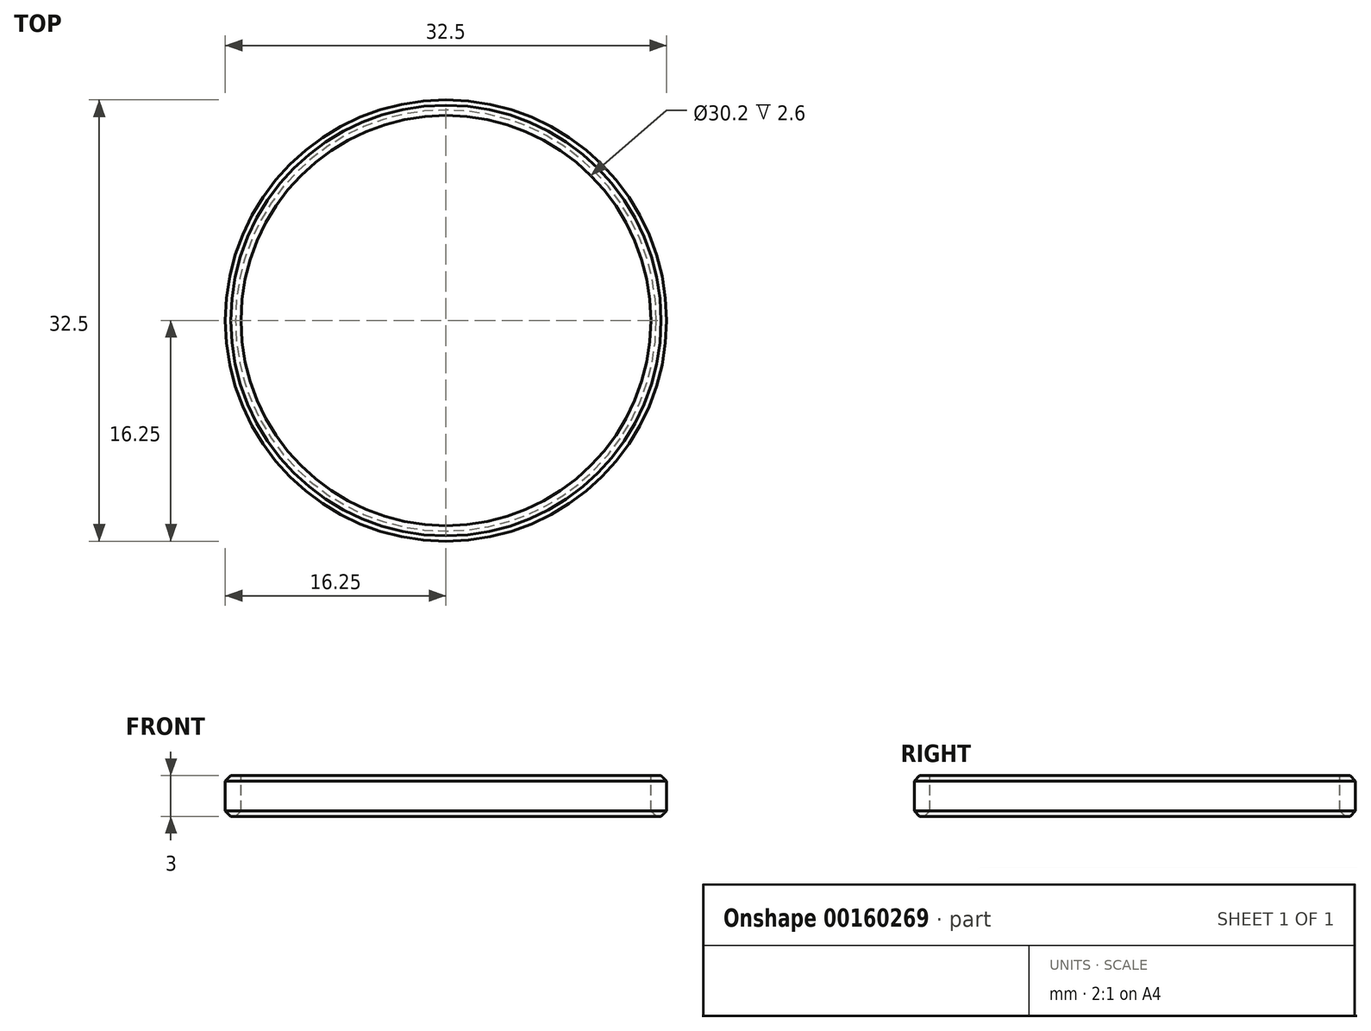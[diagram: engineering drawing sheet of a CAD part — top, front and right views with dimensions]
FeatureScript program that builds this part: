
annotation { "Feature Type Name" : "Feature", "Feature Type Description" : "" }
export const myFeature = defineFeature(function(context is Context, id is Id, definition is map)
    precondition{}
    {
        {
            var Q0;
            Q0=qCreatedBy(makeId("Top.planeOp"),FACE);
            var sketch = newSketch(context, id + "F0", { "sketchPlane" : qUnion([Q0])});
            skCircle(sketch, "E0", {"center": v(0, 0) * mm, "radius": 16.25 * mm});
            skSolve(sketch);
        }
        {
            var Q0;
            Q0 = qSketchRegion(id + "F0", true);
            extrude(context, id + "F1", {"entities" : qUnion([Q0]), "depth" : 3 * mm});
        }
        {
            var Q0;
            Q0=makeQuery(id+"F1.opExtrude","CAP_FACE",FACE,{"disambiguationData":[OSD([sQuery(id+"F0.wireOp",EDGE,"E0")])],"isStart":false});
            var sketch = newSketch(context, id + "F2", { "sketchPlane" : qUnion([Q0])});
            skCircle(sketch, "E1", {"center": v(0, 0) * mm, "radius": 15.1 * mm});
            skSolve(sketch);
        }
        {
            var Q0;
            Q0 = qSketchRegion(id + "F2", true);
            extrude(context, id + "F3", {"entities" : qUnion([Q0]), "operationType" : NewBodyOperationType.REMOVE, "endBound" : BoundingType.THROUGH_ALL, "oppositeDirection" : true, "depth" : 25 * mm});
        }
        {
            var Q0;
            Q0=makeQuery(id+"F3.boolean.opBoolean","COPY",EDGE,{"derivedFrom":makeQuery(id+"F3.opExtrude","CAP_EDGE",EDGE,{"disambiguationData":[OSD([sQuery(id+"F2.wireOp",EDGE,"E1")])],"isStart":true})});
            var Q1;
            Q1=makeQuery(id+"F3.boolean.opBoolean","INTERSECT",EDGE,{"derivedFrom":[makeQuery(id+"F1.opExtrude","CAP_FACE",FACE,{"disambiguationData":[OSD([sQuery(id+"F0.wireOp",EDGE,"E0")])],"isStart":true}),makeQuery(id+"F3.opExtrude","SWEPT_FACE",FACE,{"disambiguationData":[OSD([sQuery(id+"F2.wireOp",EDGE,"E1")])]})]});
            chamfer(context, id + "F4", {"entities" : qUnion([Q0, Q1]), "width" : 0.4 * mm, "tangentPropagation" : true});
        }
        {
            var Q0;
            Q0=makeQuery(id+"F1.opExtrude","CAP_EDGE",EDGE,{"disambiguationData":[OSD([sQuery(id+"F0.wireOp",EDGE,"E0")])],"isStart":true});
            var Q1;
            Q1=makeQuery(id+"F1.opExtrude","CAP_EDGE",EDGE,{"disambiguationData":[OSD([sQuery(id+"F0.wireOp",EDGE,"E0")])],"isStart":false});
            chamfer(context, id + "F5", {"entities" : qUnion([Q0, Q1]), "width" : 0.4 * mm, "tangentPropagation" : true});
        }
    });
